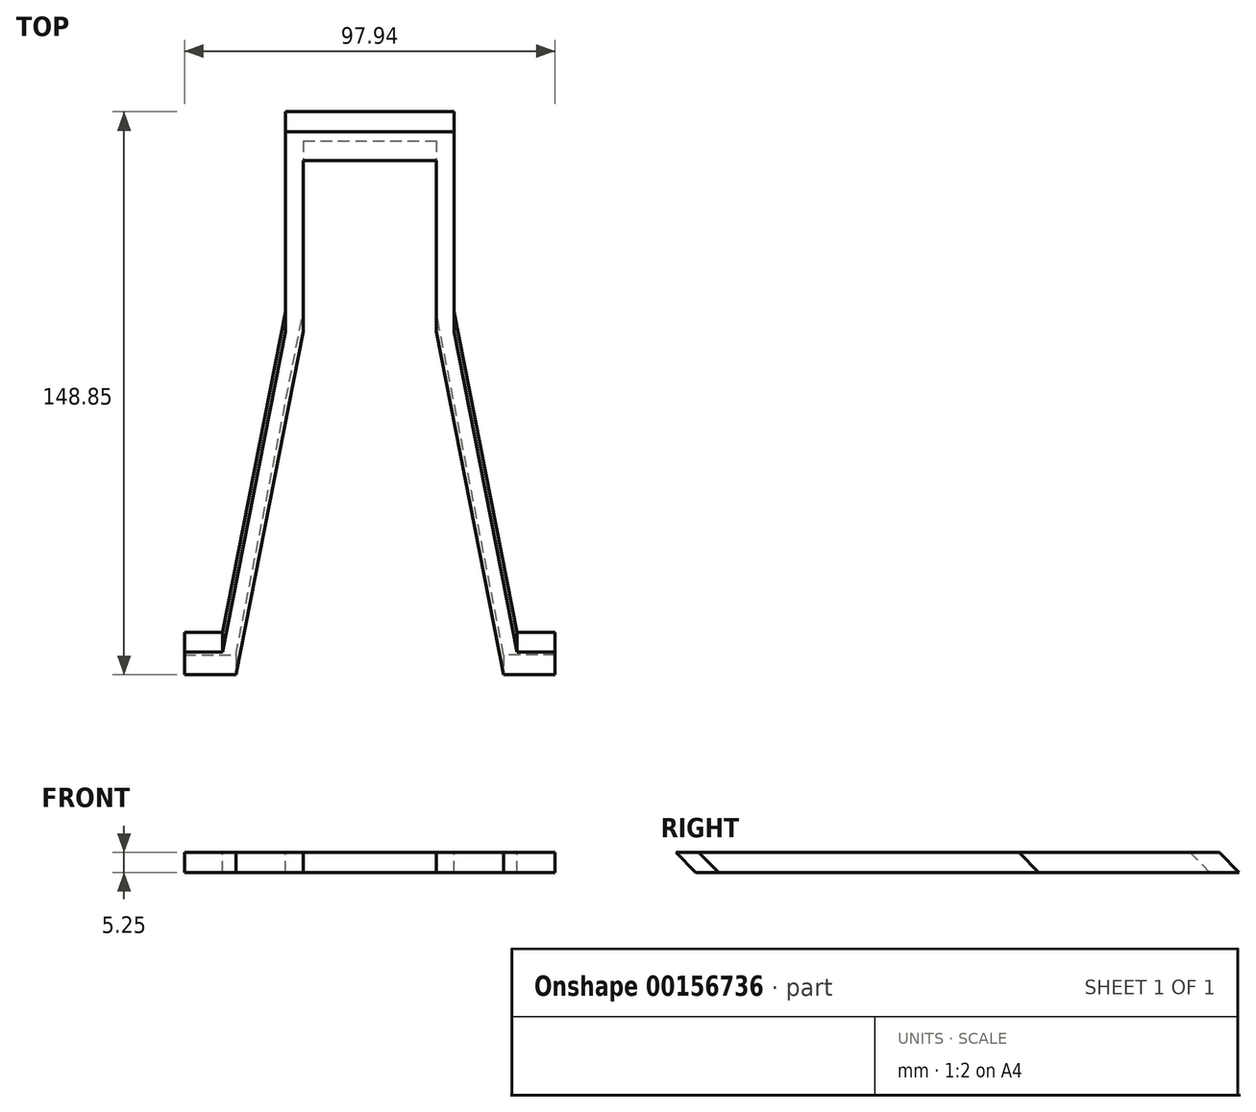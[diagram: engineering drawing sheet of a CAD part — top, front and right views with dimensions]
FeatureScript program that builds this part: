
annotation { "Feature Type Name" : "Feature", "Feature Type Description" : "" }
export const myFeature = defineFeature(function(context is Context, id is Id, definition is map)
    precondition{}
    {
        {
            var Q0;
            Q0=qCreatedBy(makeId("Top.planeOp"),FACE);
            var sketch = newSketch(context, id + "F0", { "sketchPlane" : qUnion([Q0])});
            skLineSegment(sketch, "E0.right", {"start": v(-17.58, 31.4) * mm, "end": v(-17.58, -13.86) * mm});
            skPoint(sketch, "E0.middle", {"position": v(0, 0) * mm});
            skLineSegment(sketch, "E1.0", {"start": v(-22.34, 39.1) * mm, "end": v(-22.34, -13.86) * mm});
            skLineSegment(sketch, "E2", {"start": v(-22.34, -13.86) * mm, "end": v(-38.87, -98.5) * mm});
            skLineSegment(sketch, "E3", {"start": v(-38.87, -98.5) * mm, "end": v(-48.97, -98.5) * mm});
            skLineSegment(sketch, "E4", {"start": v(-48.97, -98.5) * mm, "end": v(-48.97, -104.5) * mm});
            skLineSegment(sketch, "E5", {"start": v(-48.97, -104.5) * mm, "end": v(-38.87, -104.5) * mm});
            skLineSegment(sketch, "E6", {"start": v(-38.87, -104.5) * mm, "end": v(-35.4, -104.5) * mm});
            skLineSegment(sketch, "E7", {"start": v(-35.4, -104.5) * mm, "end": v(-17.58, -13.86) * mm});
            skLineSegment(sketch, "E8", {"start": v(-22.34, 39.1) * mm, "end": v(0, 39.1) * mm});
            skLineSegment(sketch, "E9.MirrorCS", {"start": v(38.87, -104.5) * mm, "end": v(35.4, -104.5) * mm});
            skLineSegment(sketch, "E10.MirrorCS", {"start": v(48.97, -104.5) * mm, "end": v(38.87, -104.5) * mm});
            skLineSegment(sketch, "E11.MirrorCS", {"start": v(48.97, -98.5) * mm, "end": v(48.97, -104.5) * mm});
            skLineSegment(sketch, "E12.MirrorCS", {"start": v(38.87, -98.5) * mm, "end": v(48.97, -98.5) * mm});
            skLineSegment(sketch, "E13.MirrorCS", {"start": v(22.34, -13.86) * mm, "end": v(38.87, -98.5) * mm});
            skLineSegment(sketch, "E14.MirrorCS", {"start": v(17.58, 31.4) * mm, "end": v(17.58, -13.86) * mm});
            skLineSegment(sketch, "E15.MirrorCS", {"start": v(35.4, -104.5) * mm, "end": v(17.58, -13.86) * mm});
            skLineSegment(sketch, "E16.MirrorCS", {"start": v(22.34, 39.1) * mm, "end": v(0, 39.1) * mm});
            skLineSegment(sketch, "E17.MirrorCS", {"start": v(22.34, 39.1) * mm, "end": v(22.34, -13.86) * mm});
            skLineSegment(sketch, "E18", {"start": v(-17.58, 31.4) * mm, "end": v(17.58, 31.4) * mm});
            skSolve(sketch);
        }
        {
            var Q0;
            Q0=qCreatedBy(makeId("Right.planeOp"),FACE);
            var sketch = newSketch(context, id + "F1", { "sketchPlane" : qUnion([Q0])});
            skLineSegment(sketch, "E19", {"start": v(0, 0) * mm, "end": v(-5.25, 5.25) * mm});
            skSolve(sketch);
        }
        {
            var Q0;
            Q0 = qSketchRegion(id + "F0", true);
            var Q1;
            Q1 = qConstructionFilter(qBodyType(qCreatedBy(id + "F1" ,EDGE), BodyType.WIRE), ConstructionObject.NO);
            sweep(context, id + "F2", {"profiles" : qUnion([Q0]), "path" : qUnion([Q1])});
        }
    });
